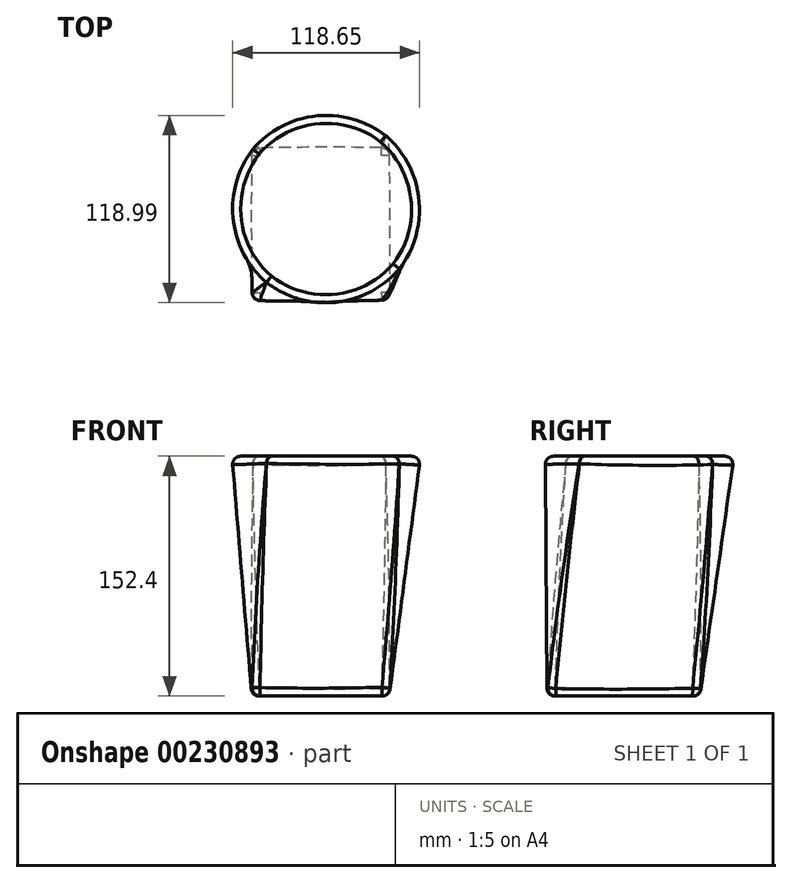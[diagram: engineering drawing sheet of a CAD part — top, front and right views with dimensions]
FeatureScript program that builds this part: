
annotation { "Feature Type Name" : "Feature", "Feature Type Description" : "" }
export const myFeature = defineFeature(function(context is Context, id is Id, definition is map)
    precondition{}
    {
        {
            var Q0;
            Q0=qCreatedBy(makeId("Top.planeOp"),FACE);
            var sketch = newSketch(context, id + "F0", { "sketchPlane" : qUnion([Q0])});
            skLineSegment(sketch, "E0.bottom", {"start": v(-47.27, 38.28) * mm, "end": v(40, 38.28) * mm});
            skLineSegment(sketch, "E0.top", {"start": v(-47.27, -58.87) * mm, "end": v(40, -58.87) * mm});
            skLineSegment(sketch, "E0.left", {"start": v(-47.27, 38.28) * mm, "end": v(-47.27, -58.87) * mm});
            skLineSegment(sketch, "E0.right", {"start": v(40, 38.28) * mm, "end": v(40, -58.87) * mm});
            skPoint(sketch, "E1", {"position": v(-47.27, -10.3) * mm});
            skSolve(sketch);
        }
        {
            var Q0;
            Q0=qCreatedBy(makeId("Top.planeOp"),FACE);
            cPlane(context, id + "F1", {"entities" : qUnion([Q0]), "cplaneType" : CPlaneType.OFFSET, "offset" : 152.4 * mm, "width" : 152.4 * mm, "height" : 152.4 * mm});
        }
        {
            var Q0;
            Q0=qCreatedBy(id+"F1.planeOp",FACE);
            var sketch = newSketch(context, id + "F2", { "sketchPlane" : qUnion([Q0])});
            skCircle(sketch, "E2", {"center": v(0, 0) * mm, "radius": 59.9 * mm});
            skSolve(sketch);
        }
        {
            var Q0;
            Q0=makeQuery(id+"F0.imprint","IMPRINT",FACE,{"disambiguationData":[TD([[makeQuery(id+"F0.imprint","IMPRINT",EDGE,{"derivedFrom":sQuery(id+"F0.wireOp",EDGE,"E0.bottom")}),-1.0]])]});
            var Q1;
            Q1=makeQuery(id+"F2.imprint","IMPRINT",FACE,{"disambiguationData":[TD([[makeQuery(id+"F2.imprint","IMPRINT",EDGE,{"derivedFrom":sQuery(id+"F2.wireOp",EDGE,"E2")}),1.0]])]});
            loft(context, id + "F3", {"sheetProfilesArray" : [{ "sheetProfileEntities" : qUnion([Q0]) }, { "sheetProfileEntities" : qUnion([Q1]) }]});
        }
        {
            var Q0;
            {var subQ0=sQuery(id+"F2.wireOp",EDGE,"E2");var subQ1=sQuery(id+"F0.wireOp",EDGE,"E0.bottom");var subQ2=sQuery(id+"F0.wireOp",EDGE,"E0.right");var subQ3=sQuery(id+"F0.wireOp",EDGE,"E0.top");var subQ4=sQuery(id+"F0.wireOp",EDGE,"E0.left");Q0=makeQuery(id+"F3.opLoft","SWEPT_FACE",FACE,{"disambiguationData":[OSD([subQ1,subQ3,subQ4,subQ2,subQ0]),TDD([makeQuery(id+"F0.imprint","INTERSECT",VERTEX,{"derivedFrom":[subQ1,subQ4]}),makeQuery(id+"F0.imprint","INTERSECT",VERTEX,{"derivedFrom":[subQ1,subQ2]}),makeQuery(id+"F0.imprint","INTERSECT",VERTEX,{"derivedFrom":[subQ3,subQ2]}),makeQuery(id+"F0.imprint","IMPRINT",EDGE,{"derivedFrom":subQ1}),makeQuery(id+"F2.imprint","IMPRINT",EDGE,{"derivedFrom":subQ0})])]});}
            var Q1;
            Q1=makeQuery(id+"F3.opLoft","SWEPT_FACE",FACE,{"disambiguationData":[OSD([sQuery(id+"F0.wireOp",EDGE,"E0.bottom"),sQuery(id+"F0.wireOp",EDGE,"E0.top"),sQuery(id+"F0.wireOp",EDGE,"E0.left"),sQuery(id+"F2.wireOp",EDGE,"E2")])]});
            var Q2;
            Q2=makeQuery(id+"F3.opLoft","CAP_FACE",FACE,{"disambiguationData":[OSD([makeQuery(id+"F2.imprint","IMPRINT",FACE,{"disambiguationData":[TD([[makeQuery(id+"F2.imprint","IMPRINT",EDGE,{"derivedFrom":sQuery(id+"F2.wireOp",EDGE,"E2")}),1.0]])]})])],"isStart":true});
            var Q3;
            Q3=makeQuery(id+"F3.opLoft","CAP_FACE",FACE,{"disambiguationData":[OSD([makeQuery(id+"F0.imprint","IMPRINT",FACE,{"disambiguationData":[TD([[makeQuery(id+"F0.imprint","IMPRINT",EDGE,{"derivedFrom":sQuery(id+"F0.wireOp",EDGE,"E0.bottom")}),-1.0]])]})])],"isStart":true});
            var Q4;
            {var subQ0=sQuery(id+"F2.wireOp",EDGE,"E2");var subQ1=sQuery(id+"F0.wireOp",EDGE,"E0.top");var subQ2=sQuery(id+"F0.wireOp",EDGE,"E0.right");var subQ3=sQuery(id+"F0.wireOp",EDGE,"E0.left");var subQ4=sQuery(id+"F0.wireOp",EDGE,"E0.bottom");Q4=makeQuery(id+"F3.opLoft","SWEPT_FACE",FACE,{"disambiguationData":[OSD([subQ4,subQ1,subQ3,subQ2,subQ0]),TDD([makeQuery(id+"F0.imprint","INTERSECT",VERTEX,{"derivedFrom":[subQ4,subQ3]}),makeQuery(id+"F0.imprint","INTERSECT",VERTEX,{"derivedFrom":[subQ1,subQ3]}),makeQuery(id+"F0.imprint","INTERSECT",VERTEX,{"derivedFrom":[subQ1,subQ2]}),makeQuery(id+"F0.imprint","IMPRINT",EDGE,{"derivedFrom":subQ1}),makeQuery(id+"F2.imprint","IMPRINT",EDGE,{"derivedFrom":subQ0})])]});}
            fillet(context, id + "F4", {"entities" : qUnion([Q0, Q1, Q2, Q3, Q4]), "radius" : 5.08 * mm, "tangentPropagation" : true, "allowEdgeOverflow" : false});
        }
    });
